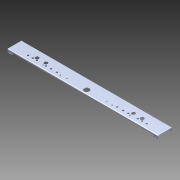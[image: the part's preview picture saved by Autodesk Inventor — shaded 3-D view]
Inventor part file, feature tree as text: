
AUTODESK INVENTOR PART (.ipt)
format: ipt  version: 2015 SP1 (Build 190203100, 203)  size: 226,816 bytes
history: native  units: in
note: dims shown in document units (in); Inventor stores cm internally (conversion verified against a paired STEP export)
features: chamfer x1, other x1, imported_body x1
ambient origin geometry x8: Origin, YZ Plane, XZ Plane, XY Plane, X Axis, Y Axis, Z Axis, Center Point
bodies: Body1 (feature_tree)
feature tree (3):
  chamfer  "Chamfer2"  [1 undecoded]
  other  "AM14U2 Outside Sheet1"
  imported_body  "Base1"
note: 1 required parameter value undecoded (feature->parameter linkage not recoverable at this tier; creation-order binding heuristic only, values carry confidence <= 0.55)
